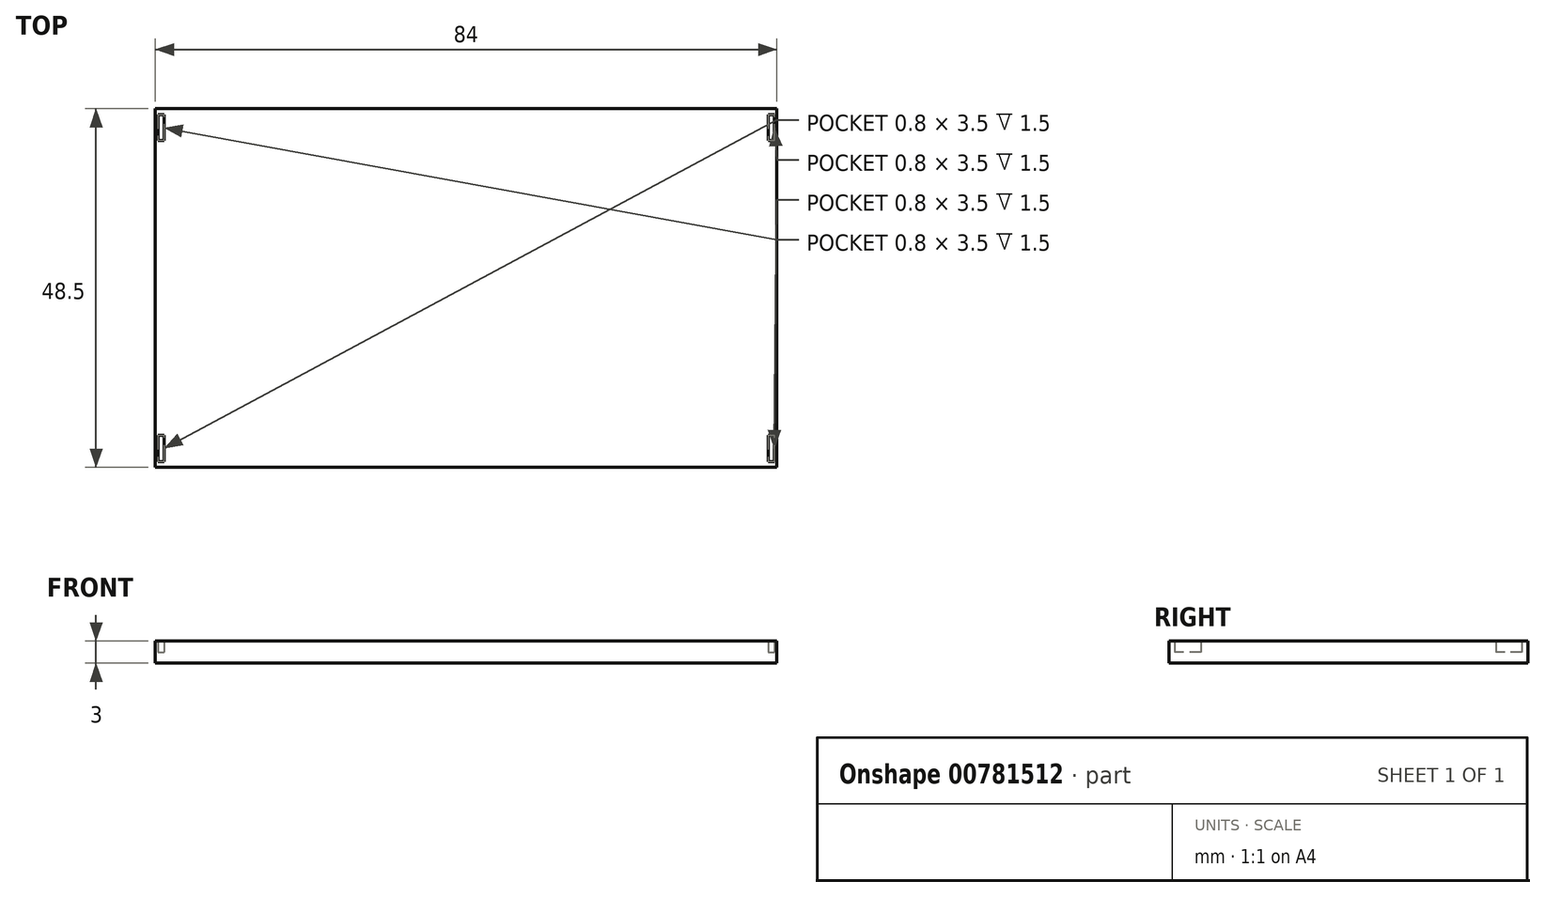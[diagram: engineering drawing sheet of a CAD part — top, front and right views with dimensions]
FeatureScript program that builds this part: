
annotation { "Feature Type Name" : "Feature", "Feature Type Description" : "" }
export const myFeature = defineFeature(function(context is Context, id is Id, definition is map)
    precondition{}
    {
        {
            var Q0;
            Q0=qCreatedBy(makeId("Top.planeOp"),FACE);
            var sketch = newSketch(context, id + "F0", { "sketchPlane" : qUnion([Q0])});
            skLineSegment(sketch, "E0.bottom", {"start": v(-42.05, 25.38) * mm, "end": v(41.95, 25.38) * mm});
            skLineSegment(sketch, "E0.top", {"start": v(-42.05, -23.12) * mm, "end": v(41.95, -23.12) * mm});
            skLineSegment(sketch, "E0.left", {"start": v(-42.05, 25.38) * mm, "end": v(-42.05, -23.12) * mm});
            skLineSegment(sketch, "E0.right", {"start": v(41.95, 25.38) * mm, "end": v(41.95, -23.12) * mm});
            skLineSegment(sketch, "E1.bottom", {"start": v(-41.7, -18.82) * mm, "end": v(-40.9, -18.82) * mm});
            skLineSegment(sketch, "E1.top", {"start": v(-41.7, -22.32) * mm, "end": v(-40.9, -22.32) * mm});
            skLineSegment(sketch, "E1.left", {"start": v(-41.7, -18.82) * mm, "end": v(-41.7, -22.32) * mm});
            skLineSegment(sketch, "E1.right", {"start": v(-40.9, -18.82) * mm, "end": v(-40.9, -22.32) * mm});
            skLineSegment(sketch, "E2.bottom", {"start": v(-41.7, 24.58) * mm, "end": v(-40.9, 24.58) * mm});
            skLineSegment(sketch, "E2.top", {"start": v(-41.7, 21.08) * mm, "end": v(-40.9, 21.08) * mm});
            skLineSegment(sketch, "E2.left", {"start": v(-41.7, 24.58) * mm, "end": v(-41.7, 21.08) * mm});
            skLineSegment(sketch, "E2.right", {"start": v(-40.9, 24.58) * mm, "end": v(-40.9, 21.08) * mm});
            skLineSegment(sketch, "E3.bottom", {"start": v(40.8, 24.58) * mm, "end": v(41.6, 24.58) * mm});
            skLineSegment(sketch, "E3.top", {"start": v(40.8, 21.08) * mm, "end": v(41.6, 21.08) * mm});
            skLineSegment(sketch, "E3.left", {"start": v(40.8, 24.58) * mm, "end": v(40.8, 21.08) * mm});
            skLineSegment(sketch, "E3.right", {"start": v(41.6, 24.58) * mm, "end": v(41.6, 21.08) * mm});
            skLineSegment(sketch, "E4.bottom", {"start": v(40.8, -18.82) * mm, "end": v(41.6, -18.82) * mm});
            skLineSegment(sketch, "E4.top", {"start": v(40.8, -22.32) * mm, "end": v(41.6, -22.32) * mm});
            skLineSegment(sketch, "E4.left", {"start": v(40.8, -18.82) * mm, "end": v(40.8, -22.32) * mm});
            skLineSegment(sketch, "E4.right", {"start": v(41.6, -18.82) * mm, "end": v(41.6, -22.32) * mm});
            skSolve(sketch);
        }
        {
            var Q0;
            Q0=qSketchRegion(id+"F0",true);
            var Q1;
            Q1=makeQuery(id+"F0.imprint","IMPRINT",FACE,{"disambiguationData":[TD([[makeQuery(id+"F0.imprint","IMPRINT",EDGE,{"derivedFrom":sQuery(id+"F0.wireOp",EDGE,"E4.bottom")}),-1.0]])]});
            var Q2;
            Q2=makeQuery(id+"F0.imprint","IMPRINT",FACE,{"disambiguationData":[TD([[makeQuery(id+"F0.imprint","IMPRINT",EDGE,{"derivedFrom":sQuery(id+"F0.wireOp",EDGE,"E3.bottom")}),-1.0]])]});
            var Q3;
            Q3=makeQuery(id+"F0.imprint","IMPRINT",FACE,{"disambiguationData":[TD([[makeQuery(id+"F0.imprint","IMPRINT",EDGE,{"derivedFrom":sQuery(id+"F0.wireOp",EDGE,"E1.bottom")}),-1.0]])]});
            var Q4;
            Q4=makeQuery(id+"F0.imprint","IMPRINT",FACE,{"disambiguationData":[TD([[makeQuery(id+"F0.imprint","IMPRINT",EDGE,{"derivedFrom":sQuery(id+"F0.wireOp",EDGE,"E2.bottom")}),-1.0]])]});
            extrude(context, id + "F1", {"entities" : qUnion([Q0, Q1, Q2, Q3, Q4]), "depth" : 3 * mm, "offsetDistance" : 25 * mm});
        }
        {
            var Q0;
            Q0=makeQuery(id+"F0.imprint","IMPRINT",FACE,{"disambiguationData":[TD([[makeQuery(id+"F0.imprint","IMPRINT",EDGE,{"derivedFrom":sQuery(id+"F0.wireOp",EDGE,"E1.bottom")}),-1.0]])]});
            var Q1;
            Q1=makeQuery(id+"F0.imprint","IMPRINT",FACE,{"disambiguationData":[TD([[makeQuery(id+"F0.imprint","IMPRINT",EDGE,{"derivedFrom":sQuery(id+"F0.wireOp",EDGE,"E2.bottom")}),-1.0]])]});
            var Q2;
            Q2=makeQuery(id+"F0.imprint","IMPRINT",FACE,{"disambiguationData":[TD([[makeQuery(id+"F0.imprint","IMPRINT",EDGE,{"derivedFrom":sQuery(id+"F0.wireOp",EDGE,"E4.bottom")}),-1.0]])]});
            var Q3;
            Q3=makeQuery(id+"F0.imprint","IMPRINT",FACE,{"disambiguationData":[TD([[makeQuery(id+"F0.imprint","IMPRINT",EDGE,{"derivedFrom":sQuery(id+"F0.wireOp",EDGE,"E3.bottom")}),-1.0]])]});
            extrude(context, id + "F2", {"entities" : qUnion([Q0, Q1, Q2, Q3]), "operationType" : NewBodyOperationType.REMOVE, "depth" : 3 * mm, "offsetDistance" : 25 * mm, "hasSecondDirection" : true, "secondDirectionOppositeDirection" : false, "secondDirectionDepth" : 1.5 * mm});
        }
    });
